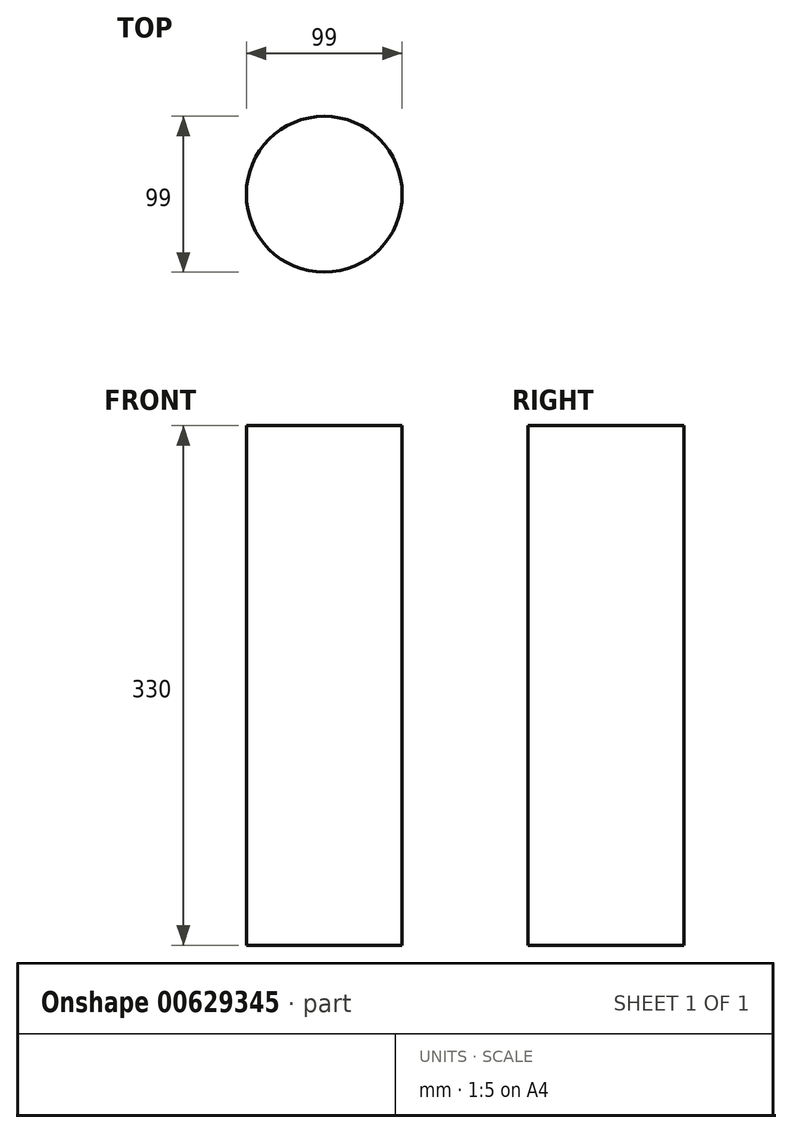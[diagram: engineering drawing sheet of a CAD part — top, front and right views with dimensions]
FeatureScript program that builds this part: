
annotation { "Feature Type Name" : "Feature", "Feature Type Description" : "" }
export const myFeature = defineFeature(function(context is Context, id is Id, definition is map)
    precondition{}
    {
        {
            var Q0;
            Q0=qCreatedBy(makeId("Top.planeOp"),FACE);
            var sketch = newSketch(context, id + "F0", { "sketchPlane" : qUnion([Q0])});
            skCircle(sketch, "E0", {"center": v(0, 0) * mm, "radius": 49.5 * mm});
            skSolve(sketch);
        }
        {
            var Q0;
            Q0 = qSketchRegion(id + "F0", true);
            extrude(context, id + "F1", {"entities" : qUnion([Q0]), "depth" : 330 * mm, "offsetDistance" : 25 * mm});
        }
    });
